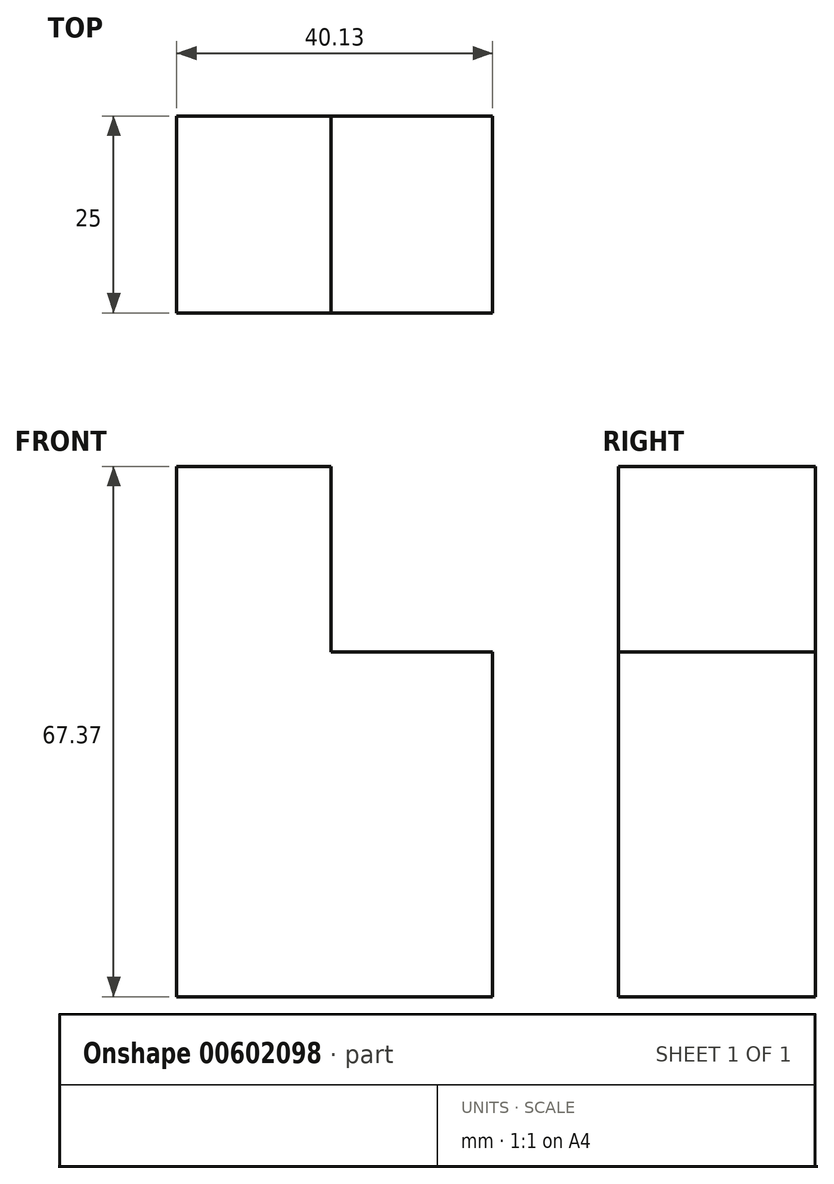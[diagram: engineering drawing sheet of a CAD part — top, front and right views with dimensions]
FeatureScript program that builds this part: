
annotation { "Feature Type Name" : "Feature", "Feature Type Description" : "" }
export const myFeature = defineFeature(function(context is Context, id is Id, definition is map)
    precondition{}
    {
        {
            var Q0;
            Q0=qCreatedBy(makeId("Front.planeOp"),FACE);
            var sketch = newSketch(context, id + "F0", { "sketchPlane" : qUnion([Q0])});
            skLineSegment(sketch, "E0", {"start": v(-37.65, 26.4) * mm, "end": v(-37.65, -34.2) * mm});
            skLineSegment(sketch, "E1", {"start": v(-37.65, -34.2) * mm, "end": v(2.48, -34.2) * mm});
            skLineSegment(sketch, "E2", {"start": v(2.48, -34.2) * mm, "end": v(2.48, 9.58) * mm});
            skLineSegment(sketch, "E3", {"start": v(2.48, 9.58) * mm, "end": v(-18.04, 9.58) * mm});
            skLineSegment(sketch, "E4", {"start": v(-18.04, 9.58) * mm, "end": v(-18.04, 26.73) * mm});
            skLineSegment(sketch, "E5", {"start": v(-37.65, 26.4) * mm, "end": v(-37.65, 33.17) * mm});
            skLineSegment(sketch, "E6", {"start": v(-18.04, 26.73) * mm, "end": v(-18.04, 33.17) * mm});
            skLineSegment(sketch, "E7", {"start": v(-37.65, 33.17) * mm, "end": v(-18.04, 33.17) * mm});
            skSolve(sketch);
        }
        {
            var Q0;
            Q0=makeQuery(id+"F0.imprint","IMPRINT",FACE,{"disambiguationData":[TD([[makeQuery(id+"F0.imprint","IMPRINT",EDGE,{"derivedFrom":sQuery(id+"F0.wireOp",EDGE,"E0")}),1.0]])]});
            extrude(context, id + "F1", {"entities" : qUnion([Q0]), "depth" : 25 * mm, "offsetDistance" : 25 * mm});
        }
    });
